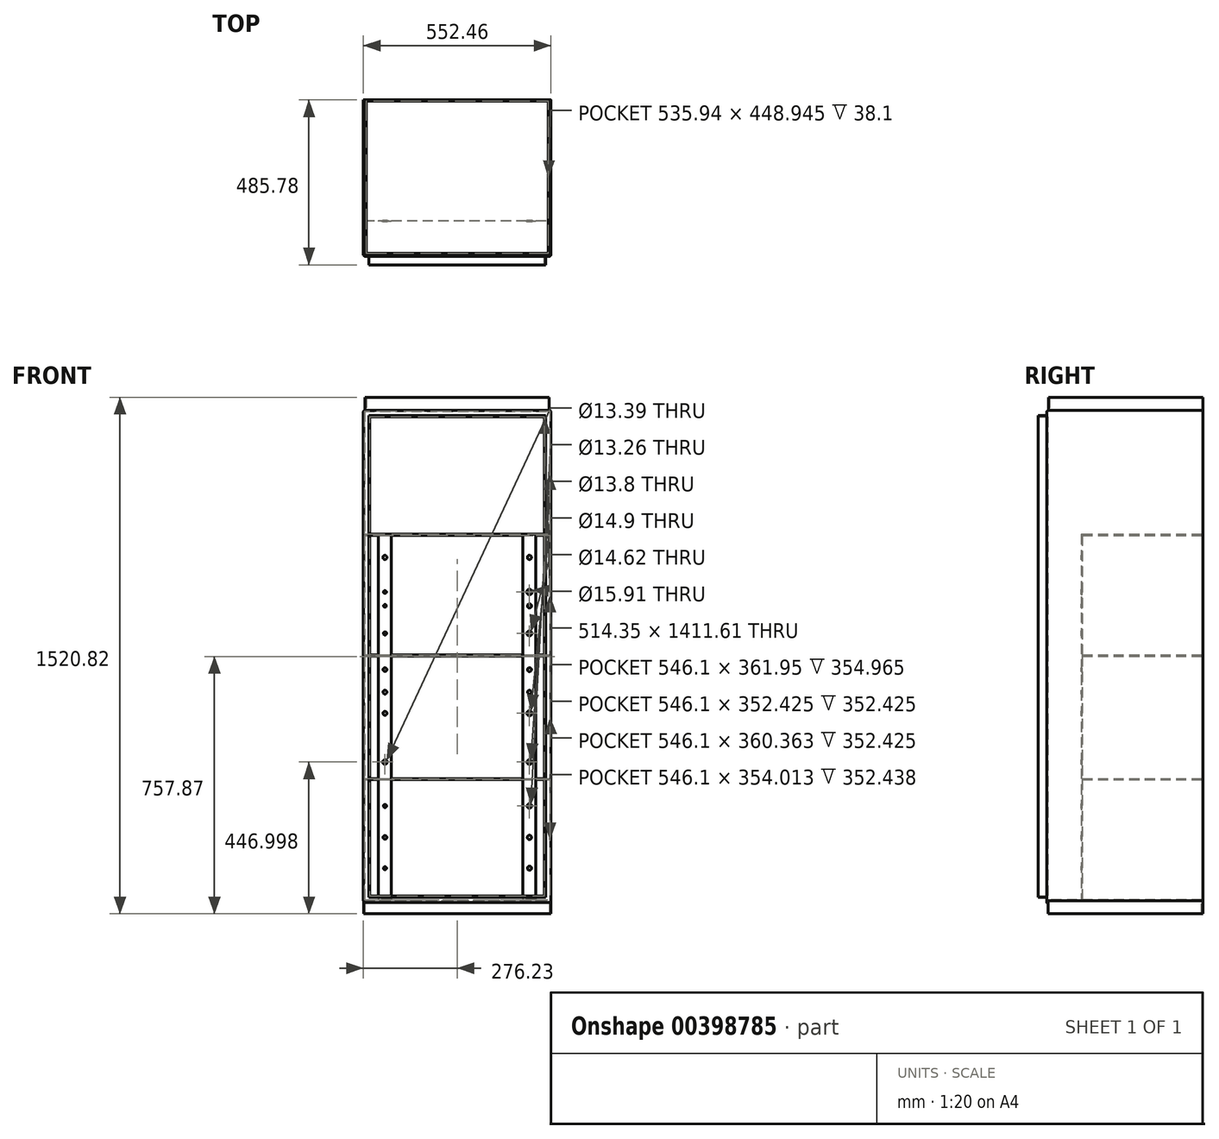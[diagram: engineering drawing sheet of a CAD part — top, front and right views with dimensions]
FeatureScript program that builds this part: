
annotation { "Feature Type Name" : "Feature", "Feature Type Description" : "" }
export const myFeature = defineFeature(function(context is Context, id is Id, definition is map)
    precondition{}
    {
        {
            var Q0;
            Q0=qCreatedBy(makeId("Front.planeOp"),FACE);
            var sketch = newSketch(context, id + "F0", { "sketchPlane" : qUnion([Q0])});
            skLineSegment(sketch, "E0.bottom", {"start": v(-273.05, 719.14) * mm, "end": v(273.05, 719.14) * mm});
            skLineSegment(sketch, "E0.top", {"start": v(-273.05, -719.14) * mm, "end": v(273.05, -719.14) * mm});
            skLineSegment(sketch, "E0.left", {"start": v(-273.05, 719.14) * mm, "end": v(-273.05, -719.14) * mm});
            skLineSegment(sketch, "E0.right", {"start": v(273.05, 719.14) * mm, "end": v(273.05, -719.14) * mm});
            skPoint(sketch, "E0.middle", {"position": v(0, 0) * mm});
            skSolve(sketch);
        }
        {
            var Q0;
            Q0 = qSketchRegion(id + "F0", true);
            extrude(context, id + "F1", {"entities" : qUnion([Q0]), "oppositeDirection" : true, "depth" : 3.17 * mm});
        }
        {
            var Q0;
            Q0=qCreatedBy(makeId("Top.planeOp"),FACE);
            cPlane(context, id + "F2", {"entities" : qUnion([Q0]), "cplaneType" : CPlaneType.OFFSET, "offset" : 719.14 * mm, "oppositeDirection" : true, "width" : 152.4 * mm, "height" : 152.4 * mm});
        }
        {
            var Q0;
            Q0=makeQuery(id+"F1.opExtrude","SWEPT_FACE",FACE,{"disambiguationData":[OSD([sQuery(id+"F0.wireOp",EDGE,"E0.right")])]});
            var sketch = newSketch(context, id + "F3", { "sketchPlane" : qUnion([Q0])});
            skLineSegment(sketch, "E1.bottom", {"start": v(3.17, 719.14) * mm, "end": v(-454.03, 719.14) * mm});
            skLineSegment(sketch, "E1.top", {"start": v(3.17, -719.14) * mm, "end": v(-454.02, -719.14) * mm});
            skLineSegment(sketch, "E1.left", {"start": v(3.18, 719.14) * mm, "end": v(3.18, -719.14) * mm});
            skLineSegment(sketch, "E1.right", {"start": v(-454.03, 719.14) * mm, "end": v(-454.02, -719.14) * mm});
            skSolve(sketch);
        }
        {
            var Q0;
            Q0 = qSketchRegion(id + "F3", true);
            extrude(context, id + "F4", {"entities" : qUnion([Q0]), "operationType" : NewBodyOperationType.ADD, "depth" : 3.17 * mm});
        }
        {
            var Q0;
            Q0=qCreatedBy(id+"F2.planeOp",FACE);
            cPlane(context, id + "F5", {"entities" : qUnion([Q0]), "cplaneType" : CPlaneType.OFFSET, "offset" : 355.6 * mm, "width" : 152.4 * mm, "height" : 152.4 * mm});
        }
        {
            var Q0;
            Q0=makeQuery(id+"F1.opExtrude","SWEPT_FACE",FACE,{"disambiguationData":[OSD([sQuery(id+"F0.wireOp",EDGE,"E0.left")])]});
            var sketch = newSketch(context, id + "F6", { "sketchPlane" : qUnion([Q0])});
            skLineSegment(sketch, "E2.bottom", {"start": v(-3.17, -719.14) * mm, "end": v(454.03, -719.14) * mm});
            skLineSegment(sketch, "E2.top", {"start": v(-3.17, 719.14) * mm, "end": v(454.02, 719.14) * mm});
            skLineSegment(sketch, "E2.left", {"start": v(-3.18, -719.14) * mm, "end": v(-3.18, 719.14) * mm});
            skLineSegment(sketch, "E2.right", {"start": v(454.03, -719.14) * mm, "end": v(454.02, 719.14) * mm});
            skSolve(sketch);
        }
        {
            var Q0;
            Q0 = qSketchRegion(id + "F6", true);
            extrude(context, id + "F7", {"entities" : qUnion([Q0]), "operationType" : NewBodyOperationType.ADD, "depth" : 3.17 * mm});
        }
        {
            var Q0;
            Q0=makeQuery(id+"F7.boolean.opBoolean","MERGE",FACE,{"derivedFrom":[makeQuery(id+"F4.boolean.opBoolean","MERGE",FACE,{"derivedFrom":[makeQuery(id+"F1.opExtrude","SWEPT_FACE",FACE,{"disambiguationData":[OSD([sQuery(id+"F0.wireOp",EDGE,"E0.top")])]}),makeQuery(id+"F4.opExtrude","SWEPT_FACE",FACE,{"disambiguationData":[OSD([sQuery(id+"F3.wireOp",EDGE,"E1.top")])]})]}),makeQuery(id+"F7.opExtrude","SWEPT_FACE",FACE,{"disambiguationData":[OSD([sQuery(id+"F6.wireOp",EDGE,"E2.bottom")])]})]});
            var sketch = newSketch(context, id + "F8", { "sketchPlane" : qUnion([Q0])});
            skLineSegment(sketch, "E3.bottom", {"start": v(-276.23, 454.03) * mm, "end": v(276.23, 454.03) * mm});
            skLineSegment(sketch, "E3.top", {"start": v(-276.23, -3.18) * mm, "end": v(276.23, -3.18) * mm});
            skLineSegment(sketch, "E3.left", {"start": v(-276.23, 454.03) * mm, "end": v(-276.23, -3.18) * mm});
            skLineSegment(sketch, "E3.right", {"start": v(276.23, 454.03) * mm, "end": v(276.23, -3.18) * mm});
            skSolve(sketch);
        }
        {
            var Q0;
            Q0 = qSketchRegion(id + "F8", true);
            extrude(context, id + "F9", {"entities" : qUnion([Q0]), "operationType" : NewBodyOperationType.ADD, "depth" : 3.17 * mm});
        }
        {
            var Q0;
            Q0=qCreatedBy(id+"F5.planeOp",FACE);
            var sketch = newSketch(context, id + "F10", { "sketchPlane" : qUnion([Q0])});
            skLineSegment(sketch, "E4.top", {"start": v(-273.05, 0) * mm, "end": v(273.05, 0) * mm});
            skLineSegment(sketch, "E4.left", {"start": v(-273.05, -352.44) * mm, "end": v(-273.05, 0) * mm});
            skLineSegment(sketch, "E4.right", {"start": v(273.05, -352.44) * mm, "end": v(273.05, 0) * mm});
            skPoint(sketch, "E5.start.orphan", {"position": v(0, 0) * mm});
            skLineSegment(sketch, "E6", {"start": v(-273.05, -352.44) * mm, "end": v(273.05, -352.44) * mm});
            skPoint(sketch, "E7.end.orphan", {"position": v(273.05, -454.03) * mm});
            skSolve(sketch);
        }
        {
            var Q0;
            Q0 = qSketchRegion(id + "F10", true);
            extrude(context, id + "F11", {"entities" : qUnion([Q0]), "operationType" : NewBodyOperationType.ADD, "endBound" : BoundingType.SYMMETRIC, "depth" : 3.17 * mm});
        }
        {
            var Q0;
            Q0=qCreatedBy(makeId("Top.planeOp"),FACE);
            var sketch = newSketch(context, id + "F12", { "sketchPlane" : qUnion([Q0])});
            skLineSegment(sketch, "E8.top", {"start": v(-273.05, 0) * mm, "end": v(273.05, 0) * mm});
            skLineSegment(sketch, "E8.left", {"start": v(-273.05, -352.43) * mm, "end": v(-273.05, 0) * mm});
            skLineSegment(sketch, "E8.right", {"start": v(273.05, -352.43) * mm, "end": v(273.05, 0) * mm});
            skPoint(sketch, "E9.start.orphan", {"position": v(0, 0) * mm});
            skLineSegment(sketch, "E10", {"start": v(-273.05, -352.43) * mm, "end": v(273.05, -352.43) * mm});
            skPoint(sketch, "E11.end.orphan", {"position": v(273.05, -454.03) * mm});
            skSolve(sketch);
        }
        {
            var Q0;
            Q0 = qSketchRegion(id + "F12", true);
            extrude(context, id + "F13", {"entities" : qUnion([Q0]), "operationType" : NewBodyOperationType.ADD, "endBound" : BoundingType.SYMMETRIC, "depth" : 3.17 * mm});
        }
        {
            var Q0;
            Q0=qCreatedBy(makeId("Top.planeOp"),FACE);
            cPlane(context, id + "F14", {"entities" : qUnion([Q0]), "cplaneType" : CPlaneType.OFFSET, "offset" : 355.6 * mm, "width" : 152.4 * mm, "height" : 152.4 * mm});
        }
        {
            var Q0;
            Q0=qCreatedBy(id+"F14.planeOp",FACE);
            var sketch = newSketch(context, id + "F15", { "sketchPlane" : qUnion([Q0])});
            skLineSegment(sketch, "E12.top", {"start": v(-273.05, 0) * mm, "end": v(273.05, 0) * mm});
            skLineSegment(sketch, "E12.left", {"start": v(-273.05, -352.43) * mm, "end": v(-273.05, 0) * mm});
            skLineSegment(sketch, "E12.right", {"start": v(273.05, -352.43) * mm, "end": v(273.05, 0) * mm});
            skPoint(sketch, "E13.start.orphan", {"position": v(0, 0) * mm});
            skLineSegment(sketch, "E14", {"start": v(-273.05, -352.43) * mm, "end": v(273.05, -352.43) * mm});
            skPoint(sketch, "E15.end.orphan", {"position": v(273.05, -454.03) * mm});
            skSolve(sketch);
        }
        {
            var Q0;
            Q0 = qSketchRegion(id + "F15", true);
            extrude(context, id + "F16", {"entities" : qUnion([Q0]), "operationType" : NewBodyOperationType.ADD, "endBound" : BoundingType.SYMMETRIC, "depth" : 3.17 * mm});
        }
        {
            var Q0;
            Q0=makeQuery(id+"F7.boolean.opBoolean","MERGE",FACE,{"derivedFrom":[makeQuery(id+"F4.boolean.opBoolean","MERGE",FACE,{"derivedFrom":[makeQuery(id+"F1.opExtrude","SWEPT_FACE",FACE,{"disambiguationData":[OSD([sQuery(id+"F0.wireOp",EDGE,"E0.bottom")])]}),makeQuery(id+"F4.opExtrude","SWEPT_FACE",FACE,{"disambiguationData":[OSD([sQuery(id+"F3.wireOp",EDGE,"E1.bottom")])]})]}),makeQuery(id+"F7.opExtrude","SWEPT_FACE",FACE,{"disambiguationData":[OSD([sQuery(id+"F6.wireOp",EDGE,"E2.top")])]})]});
            var sketch = newSketch(context, id + "F17", { "sketchPlane" : qUnion([Q0])});
            skLineSegment(sketch, "E16.bottom", {"start": v(-276.23, 3.18) * mm, "end": v(276.23, 3.18) * mm});
            skLineSegment(sketch, "E16.top", {"start": v(-276.23, -454.03) * mm, "end": v(276.23, -454.03) * mm});
            skLineSegment(sketch, "E16.left", {"start": v(-276.23, 3.18) * mm, "end": v(-276.23, -454.03) * mm});
            skLineSegment(sketch, "E16.right", {"start": v(276.23, 3.18) * mm, "end": v(276.23, -454.03) * mm});
            skSolve(sketch);
        }
        {
            var Q0;
            Q0 = qSketchRegion(id + "F17", true);
            extrude(context, id + "F18", {"entities" : qUnion([Q0]), "operationType" : NewBodyOperationType.ADD, "depth" : 3.17 * mm});
        }
        {
            var Q0;
            Q0=makeQuery(id+"F16.opExtrude","SWEPT_FACE",FACE,{"disambiguationData":[OSD([sQuery(id+"F15.wireOp",EDGE,"E14")])]});
            var sketch = newSketch(context, id + "F19", { "sketchPlane" : qUnion([Q0])});
            skLineSegment(sketch, "E17.bottom", {"start": v(-231.78, 357.19) * mm, "end": v(-193.68, 357.19) * mm});
            skLineSegment(sketch, "E17.top", {"start": v(-231.78, -719.34) * mm, "end": v(-193.68, -719.34) * mm});
            skLineSegment(sketch, "E17.left", {"start": v(-231.78, 357.19) * mm, "end": v(-231.78, -719.34) * mm});
            skLineSegment(sketch, "E17.right", {"start": v(231.78, 357.19) * mm, "end": v(231.78, -719.34) * mm});
            skLineSegment(sketch, "E18.right", {"start": v(-193.68, 357.19) * mm, "end": v(-193.68, -719.34) * mm});
            skLineSegment(sketch, "E19.bottom", {"start": v(231.78, 357.19) * mm, "end": v(193.67, 357.19) * mm});
            skLineSegment(sketch, "E19.top", {"start": v(231.78, -719.34) * mm, "end": v(193.68, -719.34) * mm});
            skLineSegment(sketch, "E19.right", {"start": v(193.67, 357.19) * mm, "end": v(193.68, -719.34) * mm});
            skLineSegment(sketch, "E20", {"start": v(-212.73, 357.19) * mm, "end": v(-212.73, -719.34) * mm});
            skLineSegment(sketch, "E21", {"start": v(212.73, -719.34) * mm, "end": v(212.72, 357.19) * mm});
            skCircle(sketch, "E22", {"center": v(-212.73, 289.1) * mm, "radius": 5.97 * mm});
            skCircle(sketch, "E23", {"center": v(-212.73, 187.3) * mm, "radius": 4.3 * mm});
            skCircle(sketch, "E24", {"center": v(-212.73, 146.5) * mm, "radius": 4.02 * mm});
            skCircle(sketch, "E25", {"center": v(-212.73, 65.32) * mm, "radius": 4.62 * mm});
            skCircle(sketch, "E26", {"center": v(-212.73, -41.25) * mm, "radius": 5.4 * mm});
            skCircle(sketch, "E27", {"center": v(-212.73, -107.57) * mm, "radius": 5.7 * mm});
            skCircle(sketch, "E28", {"center": v(-212.73, -169.83) * mm, "radius": 5.76 * mm});
            skCircle(sketch, "E29", {"center": v(-212.73, -313.41) * mm, "radius": 6.7 * mm});
            skCircle(sketch, "E30", {"center": v(-212.73, -442.79) * mm, "radius": 4.54 * mm});
            skCircle(sketch, "E31", {"center": v(-212.73, -535.23) * mm, "radius": 5.41 * mm});
            skCircle(sketch, "E32", {"center": v(-212.73, -626.06) * mm, "radius": 4.4 * mm});
            skCircle(sketch, "E33", {"center": v(212.72, 289.1) * mm, "radius": 6.15 * mm});
            skCircle(sketch, "E34", {"center": v(212.72, 187.3) * mm, "radius": 7.95 * mm});
            skCircle(sketch, "E35", {"center": v(212.72, 146.5) * mm, "radius": 6.05 * mm});
            skCircle(sketch, "E36", {"center": v(212.73, 65.32) * mm, "radius": 7.31 * mm});
            skCircle(sketch, "E37", {"center": v(212.73, -41.25) * mm, "radius": 5.83 * mm});
            skCircle(sketch, "E38", {"center": v(212.73, -107.57) * mm, "radius": 5.52 * mm});
            skCircle(sketch, "E39", {"center": v(212.73, -169.83) * mm, "radius": 7.45 * mm});
            skCircle(sketch, "E40", {"center": v(212.73, -313.41) * mm, "radius": 6.9 * mm});
            skCircle(sketch, "E41", {"center": v(212.73, -442.79) * mm, "radius": 6.63 * mm});
            skCircle(sketch, "E42", {"center": v(212.73, -535.23) * mm, "radius": 6.25 * mm});
            skCircle(sketch, "E43", {"center": v(212.73, -626.06) * mm, "radius": 6.1 * mm});
            skLineSegment(sketch, "E44.trimOffspring", {"start": v(193.67, 357.19) * mm, "end": v(231.78, 357.19) * mm});
            skLineSegment(sketch, "E45.trimOffspring", {"start": v(193.68, -719.34) * mm, "end": v(231.78, -719.34) * mm});
            skSolve(sketch);
        }
        {
            var Q0;
            Q0 = qSketchRegion(id + "F19", true);
            extrude(context, id + "F20", {"entities" : qUnion([Q0]), "operationType" : NewBodyOperationType.ADD, "depth" : 2.54 * mm});
        }
        {
            var Q0;
            Q0=makeQuery(id+"F8cfhN7xpckOiu1_1.boolean.opBoolean","MERGE",FACE,{"derivedFrom":[makeQuery(id+"FtkYPkVVSSiHgdE_1.boolean.opBoolean","MERGE",FACE,{"derivedFrom":[makeQuery(id+"F25xPrWuz19CO86_1.boolean.opBoolean","MERGE",FACE,{"derivedFrom":[makeQuery(id+"FGThUZd6UDi5DMn_1.boolean.opBoolean","MERGE",FACE,{"derivedFrom":[makeQuery(id+"FrP0hVXzfxyU2Zx_1.boolean.opBoolean","MERGE",FACE,{"derivedFrom":[makeQuery(id+"F2PBlhNORaQ0jKi_1.boolean.opBoolean","MERGE",FACE,{"derivedFrom":[makeQuery(id+"Fbj9W8a108MQZp0_1.boolean.opBoolean","MERGE",FACE,{"derivedFrom":[makeQuery(id+"F18.boolean.opBoolean","MERGE",FACE,{"derivedFrom":[makeQuery(id+"F9.boolean.opBoolean","MERGE",FACE,{"derivedFrom":[makeQuery(id+"F4.opExtrude","SWEPT_FACE",FACE,{"disambiguationData":[OSD([sQuery(id+"F3.wireOp",EDGE,"E1.right")])]}),makeQuery(id+"F7.opExtrude","SWEPT_FACE",FACE,{"disambiguationData":[OSD([sQuery(id+"F6.wireOp",EDGE,"E2.right")])]}),makeQuery(id+"F9.opExtrude","SWEPT_FACE",FACE,{"disambiguationData":[OSD([sQuery(id+"F8.wireOp",EDGE,"E3.bottom")])]})]}),makeQuery(id+"F18.opExtrude","SWEPT_FACE",FACE,{"disambiguationData":[OSD([sQuery(id+"F17.wireOp",EDGE,"E16.top")])]})]}),makeQuery(id+"Fbj9W8a108MQZp0_1.opExtrude","SWEPT_FACE",FACE,{"disambiguationData":[OSD([sQuery(id+"FeArt89PsAWOG8u_1.wireOp",EDGE,"CrmnW49H-m7cG-x491-gapm-2V8UiC6WahUY.bottom")])]}),makeQuery(id+"Fbj9W8a108MQZp0_1.opExtrude","SWEPT_FACE",FACE,{"disambiguationData":[OSD([sQuery(id+"FeArt89PsAWOG8u_1.wireOp",EDGE,"f53ec6d7-bf50-450f-826d-2aba30d25780.trimOffspring")])]}),makeQuery(id+"Fbj9W8a108MQZp0_1.opExtrude","SWEPT_FACE",FACE,{"disambiguationData":[OSD([sQuery(id+"FeArt89PsAWOG8u_1.wireOp",EDGE,"b3c58733-2030-4da8-b3f7-2ddd62a4badf.trimOffspring")])]}),makeQuery(id+"Fbj9W8a108MQZp0_1.opExtrude","SWEPT_FACE",FACE,{"disambiguationData":[OSD([sQuery(id+"FeArt89PsAWOG8u_1.wireOp",EDGE,"e155d2d0-78f3-4460-afdf-1e30193c4869.trimOffspring")])]})]}),makeQuery(id+"F2PBlhNORaQ0jKi_1.opExtrude","SWEPT_FACE",FACE,{"disambiguationData":[OSD([sQuery(id+"FcLn94Zio8bxcyp_1.wireOp",EDGE,"tt8iUhn3-dlAk-Krzh-iCTI-NRdugJWpatxm.bottom")])]})]}),makeQuery(id+"FrP0hVXzfxyU2Zx_1.opExtrude","SWEPT_FACE",FACE,{"disambiguationData":[OSD([sQuery(id+"Fgoe6NPOo1eiz6T_1.wireOp",EDGE,"DPlafmNE-YOl8-WwuC-61JN-KDi56E0OgTKs.bottom")])]})]}),makeQuery(id+"FGThUZd6UDi5DMn_1.opExtrude","SWEPT_FACE",FACE,{"disambiguationData":[OSD([sQuery(id+"FgybcaEEKl1fbRZ_1.wireOp",EDGE,"LMRK8eF3-ZzuV-1LPJ-wmcZ-5P5y7RydrIyB.bottom")])]})]}),makeQuery(id+"F25xPrWuz19CO86_1.opExtrude","SWEPT_FACE",FACE,{"disambiguationData":[OSD([sQuery(id+"FciD82uB61orVIs_1.wireOp",EDGE,"cv3iHZRK-SpjD-RgEr-M55P-mb7CsK1Lvsib.bottom")])]})]}),makeQuery(id+"FtkYPkVVSSiHgdE_1.opExtrude","SWEPT_FACE",FACE,{"disambiguationData":[OSD([sQuery(id+"FN4xGYQjz8nGnBT_1.wireOp",EDGE,"MNjkRJQt-8h5Y-qMIN-lvwj-EyhFzvfQNPQ8.bottom")])]})]}),makeQuery(id+"F8cfhN7xpckOiu1_1.opExtrude","SWEPT_FACE",FACE,{"disambiguationData":[OSD([sQuery(id+"FEVo6XwoLPaFkPh_1.wireOp",EDGE,"ZmKquLq5-uCaA-en5x-5fq1-TsXuySh0g8mG.bottom")])]})]});
            var sketch = newSketch(context, id + "F21", { "sketchPlane" : qUnion([Q0])});
            skLineSegment(sketch, "E46.bottom", {"start": v(276.23, 722.31) * mm, "end": v(-276.23, 722.31) * mm});
            skLineSegment(sketch, "E46.top", {"start": v(276.23, -727.4) * mm, "end": v(-276.23, -727.4) * mm});
            skLineSegment(sketch, "E46.left", {"start": v(276.23, 722.31) * mm, "end": v(276.23, -727.4) * mm});
            skLineSegment(sketch, "E46.right", {"start": v(-276.23, 722.31) * mm, "end": v(-276.23, -727.4) * mm});
            skLineSegment(sketch, "E47.bottom", {"start": v(-257.18, 703.26) * mm, "end": v(257.18, 703.26) * mm});
            skLineSegment(sketch, "E47.top", {"start": v(-257.17, -708.34) * mm, "end": v(257.18, -708.34) * mm});
            skLineSegment(sketch, "E47.left", {"start": v(-257.18, 703.26) * mm, "end": v(-257.17, -708.34) * mm});
            skLineSegment(sketch, "E47.right", {"start": v(257.18, 703.26) * mm, "end": v(257.18, -708.34) * mm});
            skSolve(sketch);
        }
        {
            var Q0;
            Q0 = qSketchRegion(id + "F21", true);
            extrude(context, id + "F22", {"entities" : qUnion([Q0]), "operationType" : NewBodyOperationType.ADD, "depth" : 3.17 * mm});
        }
        {
            var Q0;
            Q0=makeQuery(id+"F22.opExtrude","CAP_FACE",FACE,{"disambiguationData":[OSD([sQuery(id+"F21.wireOp",EDGE,"E46.bottom"),sQuery(id+"F21.wireOp",EDGE,"E46.top"),sQuery(id+"F21.wireOp",EDGE,"E46.left"),sQuery(id+"F21.wireOp",EDGE,"E46.right"),sQuery(id+"F21.wireOp",EDGE,"E47.bottom"),sQuery(id+"F21.wireOp",EDGE,"E47.top"),sQuery(id+"F21.wireOp",EDGE,"E47.left"),sQuery(id+"F21.wireOp",EDGE,"E47.right")])],"isStart":false});
            var sketch = newSketch(context, id + "F23", { "sketchPlane" : qUnion([Q0])});
            skLineSegment(sketch, "E48.bottom", {"start": v(-257.18, 703.26) * mm, "end": v(257.18, 703.26) * mm});
            skLineSegment(sketch, "E48.top", {"start": v(-257.18, -708.34) * mm, "end": v(257.18, -708.34) * mm});
            skLineSegment(sketch, "E48.left", {"start": v(-257.18, 703.26) * mm, "end": v(-257.18, -708.34) * mm});
            skLineSegment(sketch, "E48.right", {"start": v(257.18, 703.26) * mm, "end": v(257.18, -708.34) * mm});
            skLineSegment(sketch, "E49.bottom", {"start": v(260.35, -711.52) * mm, "end": v(-260.35, -711.52) * mm});
            skLineSegment(sketch, "E49.top", {"start": v(260.35, 706.44) * mm, "end": v(-260.35, 706.44) * mm});
            skLineSegment(sketch, "E49.left", {"start": v(260.35, -711.52) * mm, "end": v(260.35, 706.44) * mm});
            skLineSegment(sketch, "E49.right", {"start": v(-260.35, -711.52) * mm, "end": v(-260.35, 706.44) * mm});
            skSolve(sketch);
        }
        {
            var Q0;
            Q0 = qSketchRegion(id + "F23", true);
            extrude(context, id + "F24", {"entities" : qUnion([Q0]), "operationType" : NewBodyOperationType.ADD, "depth" : 25.4 * mm});
        }
        {
            var Q0;
            Q0=makeQuery(id+"F22.opExtrude","CAP_EDGE",EDGE,{"disambiguationData":[OSD([sQuery(id+"F21.wireOp",EDGE,"E46.bottom")])],"isStart":false});
            var Q1;
            Q1=makeQuery(id+"F22.opExtrude","CAP_EDGE",EDGE,{"disambiguationData":[OSD([sQuery(id+"F21.wireOp",EDGE,"E46.left")])],"isStart":false});
            var Q2;
            Q2=makeQuery(id+"F22.opExtrude","CAP_EDGE",EDGE,{"disambiguationData":[OSD([sQuery(id+"F21.wireOp",EDGE,"E46.right")])],"isStart":false});
            fillet(context, id + "F25", {"entities" : qUnion([Q0, Q1, Q2]), "radius" : 5.08 * mm, "tangentPropagation" : true, "allowEdgeOverflow" : false});
        }
        {
            var Q0;
            Q0=makeQuery(id+"F22.boolean.opBoolean","MERGE",EDGE,{"derivedFrom":[makeQuery(id+"F18.opExtrude","CAP_EDGE",EDGE,{"disambiguationData":[OSD([sQuery(id+"F17.wireOp",EDGE,"E16.right")])],"isStart":false}),makeQuery(id+"F22.opExtrude","SWEPT_EDGE",EDGE,{"disambiguationData":[OSD([sQuery(id+"F21.wireOp",EDGE,"E46.bottom"),sQuery(id+"F21.wireOp",EDGE,"E46.left")])]})]});
            var Q1;
            Q1=makeQuery(id+"F22.boolean.opBoolean","MERGE",EDGE,{"derivedFrom":[makeQuery(id+"F18.opExtrude","CAP_EDGE",EDGE,{"disambiguationData":[OSD([sQuery(id+"F17.wireOp",EDGE,"E16.left")])],"isStart":false}),makeQuery(id+"F22.opExtrude","SWEPT_EDGE",EDGE,{"disambiguationData":[OSD([sQuery(id+"F21.wireOp",EDGE,"E46.bottom"),sQuery(id+"F21.wireOp",EDGE,"E46.right")])]})]});
            fillet(context, id + "F26", {"entities" : qUnion([Q0, Q1]), "radius" : 5.08 * mm, "tangentPropagation" : true, "allowEdgeOverflow" : false});
        }
        {
            var Q0;
            Q0=makeQuery(id+"F9.opExtrude","CAP_FACE",FACE,{"disambiguationData":[OSD([sQuery(id+"F8.wireOp",EDGE,"E3.bottom"),sQuery(id+"F8.wireOp",EDGE,"E3.top"),sQuery(id+"F8.wireOp",EDGE,"E3.left"),sQuery(id+"F8.wireOp",EDGE,"E3.right")])],"isStart":false});
            var sketch = newSketch(context, id + "F27", { "sketchPlane" : qUnion([Q0])});
            skLineSegment(sketch, "E50.bottom", {"start": v(-275.66, 453.13) * mm, "end": v(275.82, 453.13) * mm});
            skLineSegment(sketch, "E50.top", {"start": v(-275.66, -2.28) * mm, "end": v(275.82, -2.28) * mm});
            skLineSegment(sketch, "E50.left", {"start": v(-275.66, 453.13) * mm, "end": v(-275.66, -2.28) * mm});
            skLineSegment(sketch, "E50.right", {"start": v(275.82, 453.13) * mm, "end": v(275.82, -2.28) * mm});
            skLineSegment(sketch, "E51.bottom", {"start": v(-271.85, 450.65) * mm, "end": v(273.64, 450.65) * mm});
            skLineSegment(sketch, "E51.top", {"start": v(-271.85, 0.8) * mm, "end": v(273.64, 0.8) * mm});
            skLineSegment(sketch, "E51.left", {"start": v(-271.85, 450.65) * mm, "end": v(-271.85, 0.8) * mm});
            skLineSegment(sketch, "E51.right", {"start": v(273.64, 450.65) * mm, "end": v(273.64, 0.8) * mm});
            skSolve(sketch);
        }
        {
            var Q0;
            Q0 = qSketchRegion(id + "F27", true);
            extrude(context, id + "F28", {"entities" : qUnion([Q0]), "operationType" : NewBodyOperationType.ADD, "depth" : 38.1 * mm});
        }
        {
            var Q0;
            Q0 = qSketchRegion(id + "F27", true);
            extrude(context, id + "F29", {"entities" : qUnion([Q0]), "operationType" : NewBodyOperationType.ADD, "depth" : 38.1 * mm});
        }
        {
            var Q0;
            Q0=makeQuery(id+"F22.boolean.opBoolean","MERGE",FACE,{"derivedFrom":[makeQuery(id+"F18.opExtrude","CAP_FACE",FACE,{"disambiguationData":[OSD([sQuery(id+"F17.wireOp",EDGE,"E16.bottom"),sQuery(id+"F17.wireOp",EDGE,"E16.top"),sQuery(id+"F17.wireOp",EDGE,"E16.left"),sQuery(id+"F17.wireOp",EDGE,"E16.right")])],"isStart":false}),makeQuery(id+"F22.opExtrude","SWEPT_FACE",FACE,{"disambiguationData":[OSD([sQuery(id+"F21.wireOp",EDGE,"E46.bottom")])]})]});
            var sketch = newSketch(context, id + "F30", { "sketchPlane" : qUnion([Q0])});
            skLineSegment(sketch, "E52.bottom", {"start": v(-271.14, 3.18) * mm, "end": v(271.15, 3.18) * mm});
            skLineSegment(sketch, "E52.top", {"start": v(-271.14, -452.12) * mm, "end": v(271.15, -452.12) * mm});
            skLineSegment(sketch, "E52.left", {"start": v(-271.14, 3.18) * mm, "end": v(-271.14, -452.12) * mm});
            skLineSegment(sketch, "E52.right", {"start": v(271.15, 3.18) * mm, "end": v(271.15, -452.12) * mm});
            skLineSegment(sketch, "E53.bottom", {"start": v(-267.97, 0) * mm, "end": v(267.97, 0) * mm});
            skLineSegment(sketch, "E53.top", {"start": v(-267.97, -448.95) * mm, "end": v(267.97, -448.95) * mm});
            skLineSegment(sketch, "E53.left", {"start": v(-267.97, 0) * mm, "end": v(-267.97, -448.95) * mm});
            skLineSegment(sketch, "E53.right", {"start": v(267.97, 0) * mm, "end": v(267.97, -448.95) * mm});
            skSolve(sketch);
        }
        {
            var Q0;
            Q0 = qSketchRegion(id + "F30", true);
            extrude(context, id + "F31", {"entities" : qUnion([Q0]), "operationType" : NewBodyOperationType.ADD, "depth" : 38.1 * mm});
        }
    });
